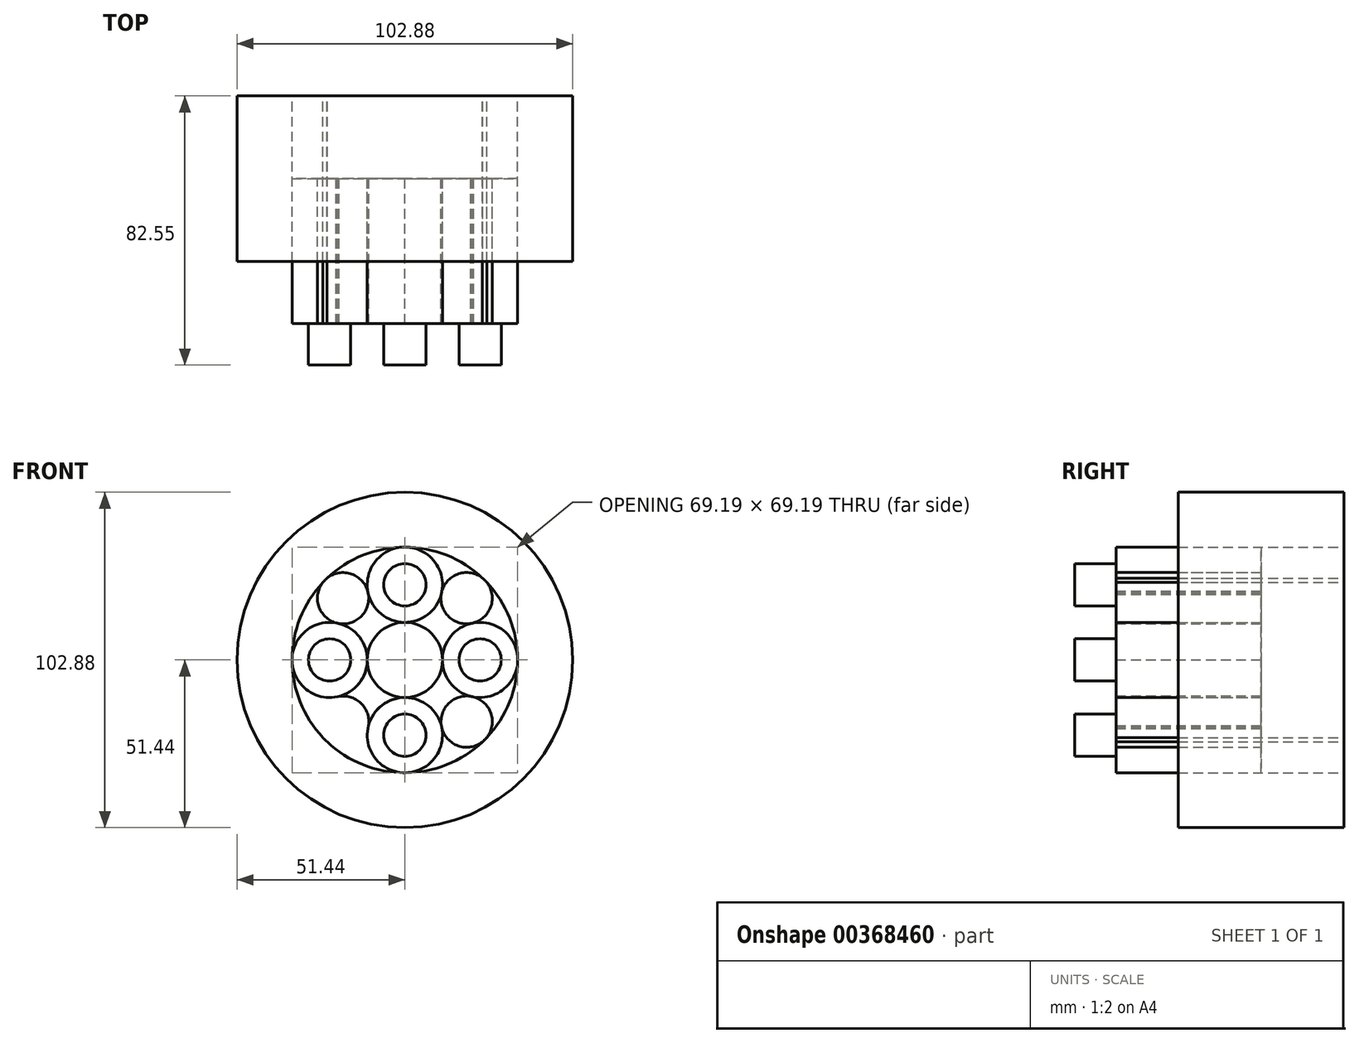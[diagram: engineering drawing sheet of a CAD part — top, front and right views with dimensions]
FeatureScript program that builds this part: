
annotation { "Feature Type Name" : "Feature", "Feature Type Description" : "" }
export const myFeature = defineFeature(function(context is Context, id is Id, definition is map)
    precondition{}
    {
        {
            var Q0;
            Q0=qCreatedBy(makeId("Front.planeOp"),FACE);
            var sketch = newSketch(context, id + "F0", { "sketchPlane" : qUnion([Q0])});
            skCircle(sketch, "E0", {"center": v(0, 0) * mm, "radius": 11.53 * mm});
            skCircle(sketch, "E1", {"center": v(0, 23.06) * mm, "radius": 11.53 * mm});
            skCircle(sketch, "E2.1.0", {"center": v(-23.06, 0) * mm, "radius": 11.53 * mm});
            skCircle(sketch, "E2.2.0", {"center": v(0, -23.06) * mm, "radius": 11.53 * mm});
            skCircle(sketch, "E2.3.0", {"center": v(23.06, 0) * mm, "radius": 11.53 * mm});
            skCircle(sketch, "E3", {"center": v(0, 0) * mm, "radius": 34.6 * mm});
            skCircle(sketch, "E4", {"center": v(0, 0) * mm, "radius": 51.44 * mm});
            skCircle(sketch, "E5", {"center": v(18.92, 18.94) * mm, "radius": 7.86 * mm});
            skPoint(sketch, "E5.first.point", {"position": v(20.68, 11.28) * mm});
            skPoint(sketch, "E5.second.point", {"position": v(11.36, 21.09) * mm});
            skPoint(sketch, "E5.third.point", {"position": v(23.8, 25.11) * mm});
            skCircle(sketch, "E6.1.0", {"center": v(-18.94, 18.92) * mm, "radius": 7.86 * mm});
            skCircle(sketch, "E6.2.0", {"center": v(-18.92, -18.94) * mm, "radius": 7.86 * mm});
            skCircle(sketch, "E6.3.0", {"center": v(18.94, -18.92) * mm, "radius": 7.86 * mm});
            skCircle(sketch, "E7", {"center": v(23.06, 0) * mm, "radius": 6.48 * mm});
            skCircle(sketch, "E8.1.0", {"center": v(0, 23.06) * mm, "radius": 6.48 * mm});
            skCircle(sketch, "E8.2.0", {"center": v(-23.06, 0) * mm, "radius": 6.48 * mm});
            skCircle(sketch, "E8.3.0", {"center": v(0, -23.06) * mm, "radius": 6.48 * mm});
            skSolve(sketch);
        }
        {
            var Q0;
            Q0=makeQuery(id+"F0.imprint","IMPRINT",FACE,{"disambiguationData":[TD([[makeQuery(id+"F0.imprint","IMPRINT",EDGE,{"derivedFrom":sQuery(id+"F0.wireOp",EDGE,"E8.1.0")}),-1.0]])]});
            extrude(context, id + "F1", {"entities" : qUnion([Q0]), "depth" : 44.45 * mm});
        }
        {
            var Q0;
            Q0=makeQuery(id+"F0.imprint","IMPRINT",FACE,{"disambiguationData":[TD([[makeQuery(id+"F0.imprint","IMPRINT",EDGE,{"derivedFrom":sQuery(id+"F0.wireOp",EDGE,"E8.1.0")}),1.0]])]});
            extrude(context, id + "F2", {"entities" : qUnion([Q0]), "operationType" : NewBodyOperationType.ADD, "depth" : 57.15 * mm});
        }
        {
            var Q0;
            Q0=makeQuery(id+"F0.imprint","IMPRINT",FACE,{"disambiguationData":[TD([[makeQuery(id+"F0.imprint","IMPRINT",EDGE,{"derivedFrom":sQuery(id+"F0.wireOp",EDGE,"E8.2.0")}),-1.0]])]});
            extrude(context, id + "F3", {"entities" : qUnion([Q0]), "depth" : 44.45 * mm});
        }
        {
            var Q0;
            Q0=makeQuery(id+"F0.imprint","IMPRINT",FACE,{"disambiguationData":[TD([[makeQuery(id+"F0.imprint","IMPRINT",EDGE,{"derivedFrom":sQuery(id+"F0.wireOp",EDGE,"E8.2.0")}),1.0]])]});
            extrude(context, id + "F4", {"entities" : qUnion([Q0]), "operationType" : NewBodyOperationType.ADD, "depth" : 57.15 * mm});
        }
        {
            var Q0;
            {var subQ0=sQuery(id+"F0.wireOp",EDGE,"E6.2.0");var subQ7=sQuery(id+"F0.wireOp",EDGE,"E2.1.0");var subQ8=makeQuery(id+"F0.imprint","INTERSECT",VERTEX,{"disambiguationData":[OD(0.0)],"derivedFrom":[subQ7,subQ0]});Q0=makeQuery(id+"F0.imprint","IMPRINT",FACE,{"disambiguationData":[TD([[makeQuery(id+"F0.imprint","IMPRINT",EDGE,{"disambiguationData":[TD([[subQ8,-1.0]])],"derivedFrom":subQ7}),-1.0]])]});}
            extrude(context, id + "F5", {"entities" : qUnion([Q0]), "depth" : 44.45 * mm});
        }
        {
            var Q0;
            {var subQ0=sQuery(id+"F0.wireOp",EDGE,"E6.1.0");var subQ7=sQuery(id+"F0.wireOp",EDGE,"E1");var subQ8=makeQuery(id+"F0.imprint","INTERSECT",VERTEX,{"disambiguationData":[OD(0.0)],"derivedFrom":[subQ7,subQ0]});Q0=makeQuery(id+"F0.imprint","IMPRINT",FACE,{"disambiguationData":[TD([[makeQuery(id+"F0.imprint","IMPRINT",EDGE,{"disambiguationData":[TD([[subQ8,-1.0]])],"derivedFrom":subQ7}),-1.0]])]});}
            extrude(context, id + "F6", {"entities" : qUnion([Q0]), "depth" : 44.45 * mm});
        }
        {
            var Q0;
            {var subQ0=sQuery(id+"F0.wireOp",EDGE,"E6.3.0");var subQ7=sQuery(id+"F0.wireOp",EDGE,"E2.2.0");var subQ8=makeQuery(id+"F0.imprint","INTERSECT",VERTEX,{"disambiguationData":[OD(0.0)],"derivedFrom":[subQ7,subQ0]});Q0=makeQuery(id+"F0.imprint","IMPRINT",FACE,{"disambiguationData":[TD([[makeQuery(id+"F0.imprint","IMPRINT",EDGE,{"disambiguationData":[TD([[subQ8,-1.0]])],"derivedFrom":subQ7}),-1.0]])]});}
            extrude(context, id + "F7", {"entities" : qUnion([Q0]), "depth" : 44.45 * mm});
        }
        {
            var Q0;
            {var subQ0=sQuery(id+"F0.wireOp",EDGE,"E5");var subQ1=sQuery(id+"F0.wireOp",EDGE,"E1");var subQ9=makeQuery(id+"F0.imprint","INTERSECT",VERTEX,{"disambiguationData":[OD(0.0)],"derivedFrom":[subQ1,subQ0]});Q0=makeQuery(id+"F0.imprint","IMPRINT",FACE,{"disambiguationData":[TD([[makeQuery(id+"F0.imprint","IMPRINT",EDGE,{"disambiguationData":[TD([[subQ9,-1.0]])],"derivedFrom":subQ1}),-1.0]])]});}
            extrude(context, id + "F8", {"entities" : qUnion([Q0]), "depth" : 44.45 * mm});
        }
        {
            var Q0;
            Q0=makeQuery(id+"F0.imprint","IMPRINT",FACE,{"disambiguationData":[TD([[makeQuery(id+"F0.imprint","IMPRINT",EDGE,{"derivedFrom":sQuery(id+"F0.wireOp",EDGE,"E7")}),-1.0]])]});
            extrude(context, id + "F9", {"entities" : qUnion([Q0]), "depth" : 44.45 * mm});
        }
        {
            var Q0;
            Q0=makeQuery(id+"F0.imprint","IMPRINT",FACE,{"disambiguationData":[TD([[makeQuery(id+"F0.imprint","IMPRINT",EDGE,{"derivedFrom":sQuery(id+"F0.wireOp",EDGE,"E7")}),1.0]])]});
            extrude(context, id + "F10", {"entities" : qUnion([Q0]), "operationType" : NewBodyOperationType.ADD, "depth" : 57.15 * mm});
        }
        {
            var Q0;
            Q0=makeQuery(id+"F0.imprint","IMPRINT",FACE,{"disambiguationData":[TD([[makeQuery(id+"F0.imprint","IMPRINT",EDGE,{"derivedFrom":sQuery(id+"F0.wireOp",EDGE,"E8.3.0")}),-1.0]])]});
            extrude(context, id + "F11", {"entities" : qUnion([Q0]), "depth" : 44.45 * mm});
        }
        {
            var Q0;
            Q0=makeQuery(id+"F0.imprint","IMPRINT",FACE,{"disambiguationData":[TD([[makeQuery(id+"F0.imprint","IMPRINT",EDGE,{"derivedFrom":sQuery(id+"F0.wireOp",EDGE,"E8.3.0")}),1.0]])]});
            extrude(context, id + "F12", {"entities" : qUnion([Q0]), "operationType" : NewBodyOperationType.ADD, "depth" : 57.15 * mm});
        }
        {
            var Q0;
            {var subQ0=sQuery(id+"F0.wireOp",EDGE,"E0");var subQ1=makeQuery(id+"F0.imprint","INTERSECT",VERTEX,{"derivedFrom":[subQ0,sQuery(id+"F0.wireOp",EDGE,"E1")]});Q0=makeQuery(id+"F0.imprint","IMPRINT",FACE,{"disambiguationData":[TD([[makeQuery(id+"F0.imprint","IMPRINT",EDGE,{"disambiguationData":[TD([[subQ1,1.0]])],"derivedFrom":subQ0}),1.0]])]});}
            extrude(context, id + "F13", {"entities" : qUnion([Q0]), "depth" : 44.45 * mm});
        }
        {
            var Q0;
            Q0=makeQuery(id+"F0.imprint","IMPRINT",FACE,{"disambiguationData":[TD([[makeQuery(id+"F0.imprint","IMPRINT",EDGE,{"derivedFrom":sQuery(id+"F0.wireOp",EDGE,"E4")}),1.0]])]});
            extrude(context, id + "F14", {"entities" : qUnion([Q0]), "depth" : 25.4 * mm, "hasSecondDirection" : true, "secondDirectionOppositeDirection" : true, "secondDirectionDepth" : 25.4 * mm});
        }
    });
